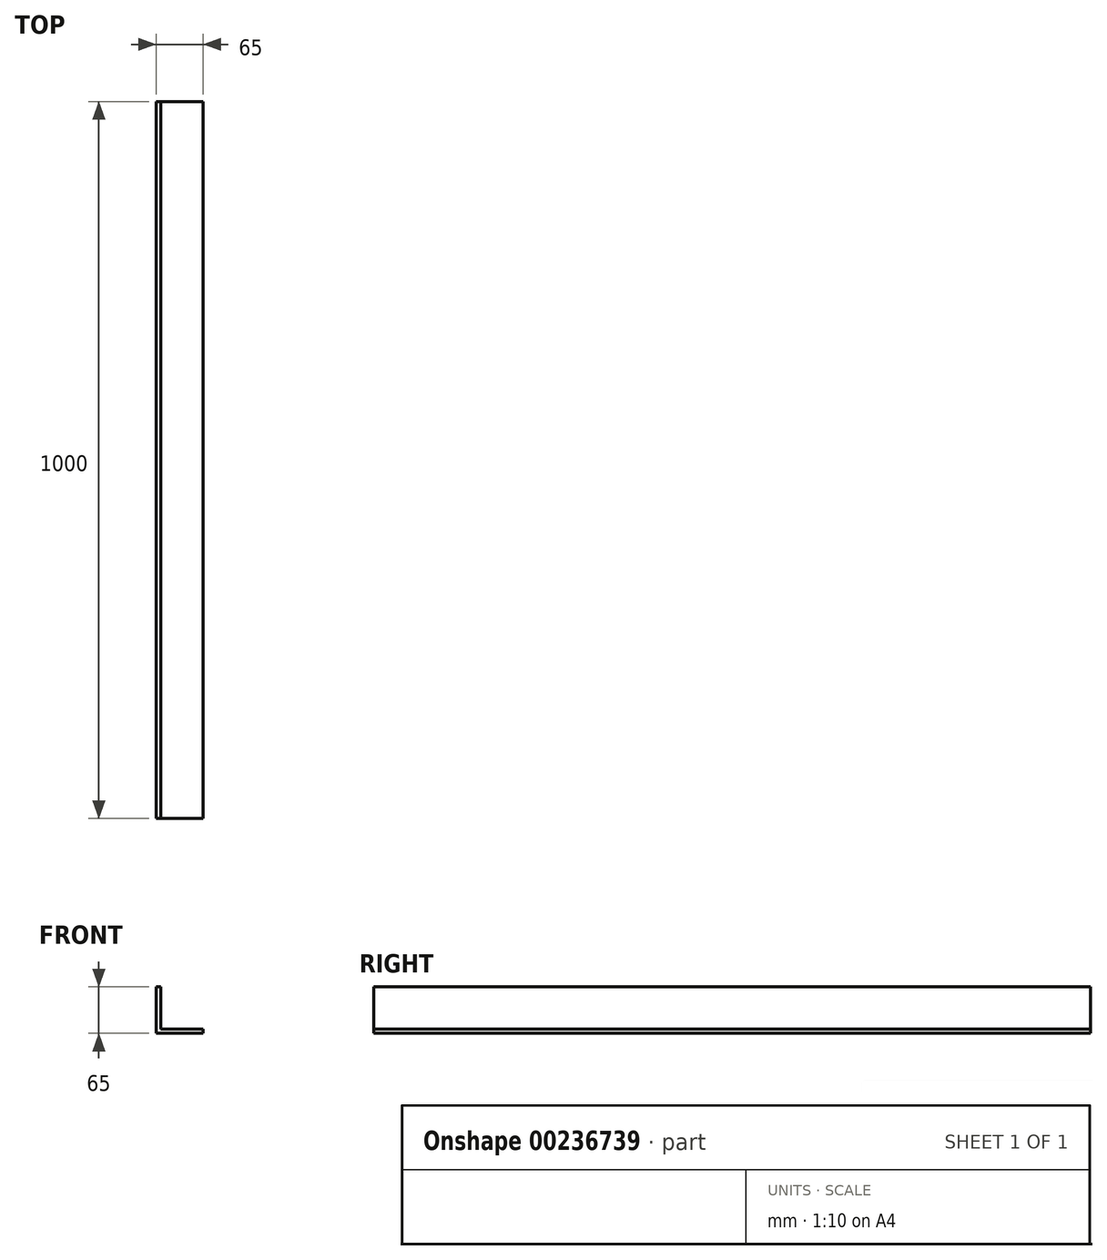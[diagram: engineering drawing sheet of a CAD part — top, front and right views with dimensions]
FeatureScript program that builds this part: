
annotation { "Feature Type Name" : "Feature", "Feature Type Description" : "" }
export const myFeature = defineFeature(function(context is Context, id is Id, definition is map)
    precondition{}
    {
        {
            var Q0;
            Q0=qCreatedBy(makeId("Front.planeOp"),FACE);
            var sketch = newSketch(context, id + "F0", { "sketchPlane" : qUnion([Q0])});
            skLineSegment(sketch, "E0.bottom", {"start": v(0, 0) * mm, "end": v(-6, 0) * mm});
            skLineSegment(sketch, "E0.top", {"start": v(0, 65) * mm, "end": v(-6, 65) * mm});
            skLineSegment(sketch, "E0.left", {"start": v(0, 6) * mm, "end": v(0, 65) * mm});
            skLineSegment(sketch, "E0.right", {"start": v(-6, 0) * mm, "end": v(-6, 65) * mm});
            skLineSegment(sketch, "E1.bottom", {"start": v(0, 0) * mm, "end": v(59, 0) * mm});
            skLineSegment(sketch, "E1.top", {"start": v(0, 6) * mm, "end": v(59, 6) * mm});
            skLineSegment(sketch, "E1.right", {"start": v(59, 0) * mm, "end": v(59, 6) * mm});
            skSolve(sketch);
        }
        {
            var Q0;
            Q0=makeQuery(id+"F0.imprint","IMPRINT",FACE,{"disambiguationData":[TD([[makeQuery(id+"F0.imprint","IMPRINT",EDGE,{"derivedFrom":sQuery(id+"F0.wireOp",EDGE,"E0.bottom")}),-1.0]])]});
            extrude(context, id + "F1", {"entities" : qUnion([Q0]), "depth" : 1000 * mm, "offsetDistance" : 25 * mm});
        }
    });
